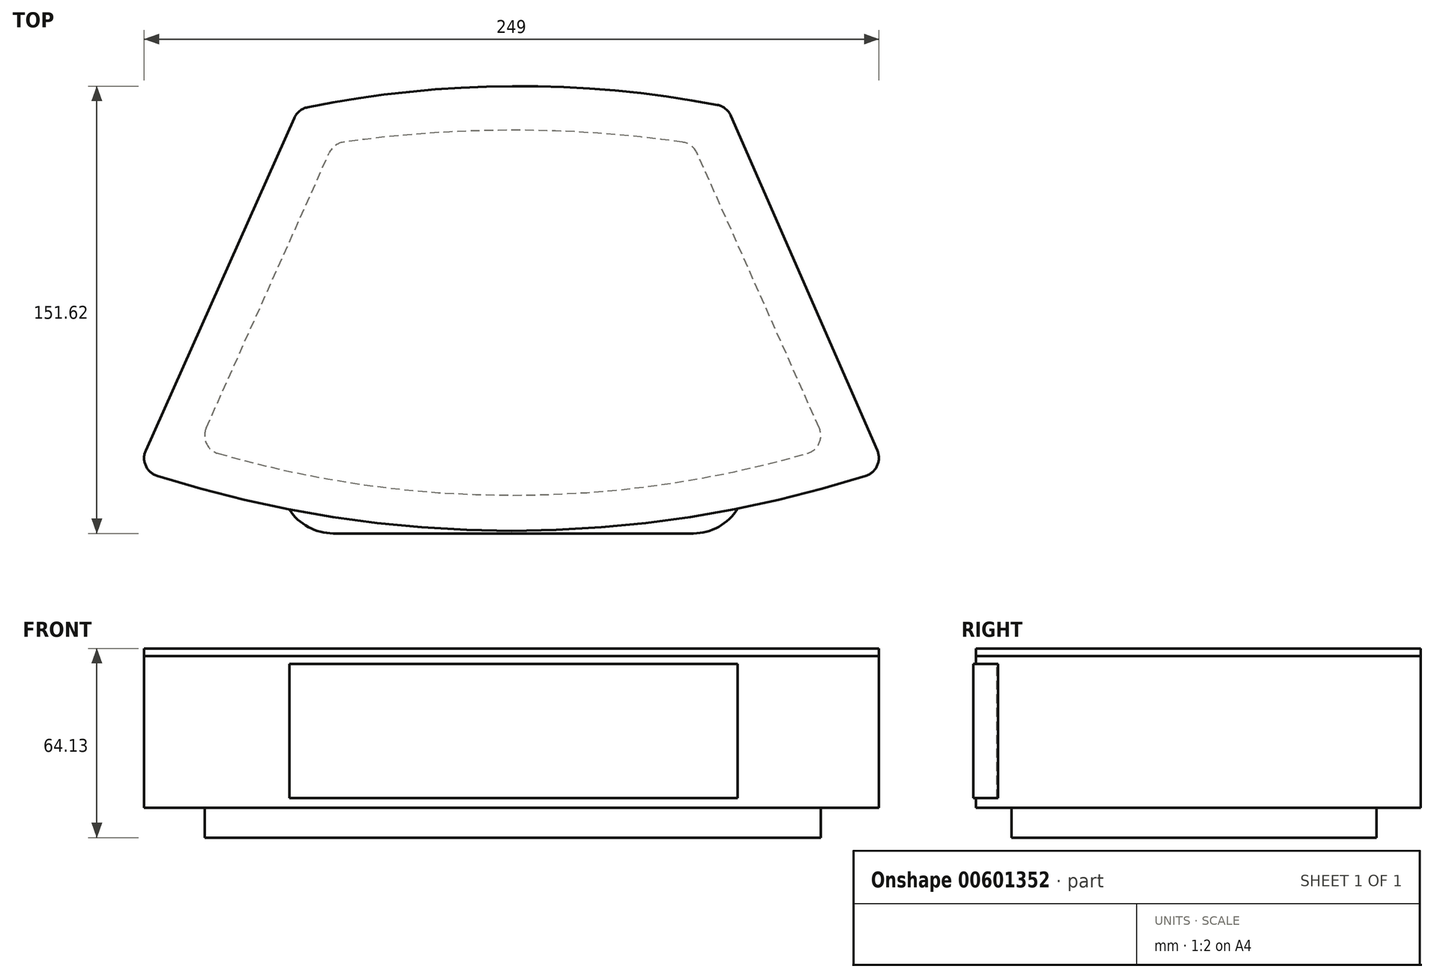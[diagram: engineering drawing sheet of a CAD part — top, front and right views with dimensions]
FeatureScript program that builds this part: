
annotation { "Feature Type Name" : "Feature", "Feature Type Description" : "" }
export const myFeature = defineFeature(function(context is Context, id is Id, definition is map)
    precondition{}
    {
        {
            var Q0;
            Q0=qCreatedBy(makeId("Top.planeOp"),FACE);
            var sketch = newSketch(context, id + "F0", { "sketchPlane" : qUnion([Q0])});
            skLineSegment(sketch, "E0", {"start": v(-72.1, 72.44) * mm, "end": v(-126.63, -49.66) * mm});
            skLineSegment(sketch, "E1", {"start": v(73.23, 73.26) * mm, "end": v(126.96, -49.66) * mm});
            skArc(sketch, "E2", {"start": v(-126.63, -49.66) * mm, "mid": v(0.16, -70.49) * mm, "end": v(126.96, -49.66) * mm});
            skArc(sketch, "E3", {"start": v(73.23, 73.26) * mm, "mid": v(0.52, 80.25) * mm, "end": v(-72.1, 72.44) * mm});
            skSolve(sketch);
        }
        {
            var Q0;
            Q0 = qSketchRegion(id + "F0", true);
            extrude(context, id + "F1", {"entities" : qUnion([Q0]), "oppositeDirection" : true, "depth" : 51.43 * mm, "offsetDistance" : 25.4 * mm});
        }
        {
            var Q0;
            Q0=makeQuery(id+"F1.opExtrude","CAP_FACE",FACE,{"disambiguationData":[OSD([sQuery(id+"F0.wireOp",EDGE,"E0"),sQuery(id+"F0.wireOp",EDGE,"E1"),sQuery(id+"F0.wireOp",EDGE,"E2"),sQuery(id+"F0.wireOp",EDGE,"E3")])],"isStart":false});
            var sketch = newSketch(context, id + "F2", { "sketchPlane" : qUnion([Q0])});
            skLineSegment(sketch, "E4", {"start": v(-106.2, 42.2) * mm, "end": v(-60.18, -60.78) * mm});
            skArc(sketch, "E5", {"start": v(-60.18, -60.78) * mm, "mid": v(0.75, -65.32) * mm, "end": v(61.68, -60.78) * mm});
            skLineSegment(sketch, "E6", {"start": v(107.41, 42.2) * mm, "end": v(61.68, -60.78) * mm});
            skArc(sketch, "E7", {"start": v(107.41, 42.2) * mm, "mid": v(0.6, 58.42) * mm, "end": v(-106.2, 42.2) * mm});
            skSolve(sketch);
        }
        {
            var Q0;
            Q0 = qSketchRegion(id + "F2", true);
            extrude(context, id + "F3", {"entities" : qUnion([Q0]), "depth" : 10.16 * mm, "offsetDistance" : 25.4 * mm});
        }
        {
            var Q0;
            Q0=makeQuery(id+"F1.opExtrude","CAP_FACE",FACE,{"disambiguationData":[OSD([sQuery(id+"F0.wireOp",EDGE,"E0"),sQuery(id+"F0.wireOp",EDGE,"E1"),sQuery(id+"F0.wireOp",EDGE,"E2"),sQuery(id+"F0.wireOp",EDGE,"E3")])],"isStart":true});
            var sketch = newSketch(context, id + "F4", { "sketchPlane" : qUnion([Q0])});
            skSolve(sketch);
        }
        {
            var Q0;
            Q0=makeQuery(id+"F4.imprint","IMPRINT",FACE,{"disambiguationData":[TD([[makeQuery(id+"F4.imprint","IMPRINT",EDGE,{"derivedFrom":makeQuery(id+"F1.opExtrude","CAP_EDGE",EDGE,{"disambiguationData":[OSD([sQuery(id+"F0.wireOp",EDGE,"E0")])],"isStart":true})}),1.0]])]});
            extrude(context, id + "F5", {"entities" : qUnion([Q0]), "depth" : 2.54 * mm, "offsetDistance" : 25.4 * mm});
        }
        {
            var Q0;
            Q0=makeQuery(id+"F1.opExtrude","SWEPT_EDGE",EDGE,{"disambiguationData":[OSD([sQuery(id+"F0.wireOp",EDGE,"E0"),sQuery(id+"F0.wireOp",EDGE,"E2")])]});
            var Q1;
            Q1=makeQuery(id+"F5.opExtrude","SWEPT_EDGE",EDGE,{"disambiguationData":[OSD([sQuery(id+"F0.wireOp",EDGE,"E0"),sQuery(id+"F0.wireOp",EDGE,"E2")])]});
            var Q2;
            Q2=makeQuery(id+"F3.opExtrude","SWEPT_EDGE",EDGE,{"disambiguationData":[OSD([sQuery(id+"F2.wireOp",EDGE,"E4"),sQuery(id+"F2.wireOp",EDGE,"E7")])]});
            var Q3;
            Q3=makeQuery(id+"F5.opExtrude","SWEPT_EDGE",EDGE,{"disambiguationData":[OSD([sQuery(id+"F0.wireOp",EDGE,"E1"),sQuery(id+"F0.wireOp",EDGE,"E2")])]});
            var Q4;
            Q4=makeQuery(id+"F1.opExtrude","SWEPT_EDGE",EDGE,{"disambiguationData":[OSD([sQuery(id+"F0.wireOp",EDGE,"E1"),sQuery(id+"F0.wireOp",EDGE,"E2")])]});
            var Q5;
            Q5=makeQuery(id+"F3.opExtrude","SWEPT_EDGE",EDGE,{"disambiguationData":[OSD([sQuery(id+"F2.wireOp",EDGE,"E6"),sQuery(id+"F2.wireOp",EDGE,"E7")])]});
            var Q6;
            Q6=makeQuery(id+"F5.opExtrude","SWEPT_EDGE",EDGE,{"disambiguationData":[OSD([sQuery(id+"F0.wireOp",EDGE,"E1"),sQuery(id+"F0.wireOp",EDGE,"E3")])]});
            var Q7;
            Q7=makeQuery(id+"F1.opExtrude","SWEPT_EDGE",EDGE,{"disambiguationData":[OSD([sQuery(id+"F0.wireOp",EDGE,"E1"),sQuery(id+"F0.wireOp",EDGE,"E3")])]});
            var Q8;
            Q8=makeQuery(id+"F3.opExtrude","SWEPT_EDGE",EDGE,{"disambiguationData":[OSD([sQuery(id+"F2.wireOp",EDGE,"E5"),sQuery(id+"F2.wireOp",EDGE,"E6")])]});
            var Q9;
            Q9=makeQuery(id+"F5.opExtrude","SWEPT_EDGE",EDGE,{"disambiguationData":[OSD([sQuery(id+"F0.wireOp",EDGE,"E0"),sQuery(id+"F0.wireOp",EDGE,"E3")])]});
            var Q10;
            Q10=makeQuery(id+"F1.opExtrude","SWEPT_EDGE",EDGE,{"disambiguationData":[OSD([sQuery(id+"F0.wireOp",EDGE,"E0"),sQuery(id+"F0.wireOp",EDGE,"E3")])]});
            var Q11;
            Q11=makeQuery(id+"F3.opExtrude","SWEPT_EDGE",EDGE,{"disambiguationData":[OSD([sQuery(id+"F2.wireOp",EDGE,"E4"),sQuery(id+"F2.wireOp",EDGE,"E5")])]});
            fillet(context, id + "F6", {"entities" : qUnion([Q0, Q1, Q2, Q3, Q4, Q5, Q6, Q7, Q8, Q9, Q10, Q11]), "radius" : 6.35 * mm, "tangentPropagation" : true, "allowEdgeOverflow" : false});
        }
        {
            var Q0;
            Q0=qCreatedBy(makeId("Front.planeOp"),FACE);
            var sketch = newSketch(context, id + "F7", { "sketchPlane" : qUnion([Q0])});
            skLineSegment(sketch, "E8", {"start": v(-75.07, -2.73) * mm, "end": v(-75.07, -48.2) * mm});
            skLineSegment(sketch, "E9", {"start": v(-75.07, -48.2) * mm, "end": v(76.89, -48.2) * mm});
            skLineSegment(sketch, "E10", {"start": v(76.89, -48.2) * mm, "end": v(76.89, -2.73) * mm});
            skLineSegment(sketch, "E11", {"start": v(76.89, -2.73) * mm, "end": v(-75.07, -2.73) * mm});
            skSolve(sketch);
        }
        {
            var Q0;
            Q0 = qSketchRegion(id + "F7", true);
            extrude(context, id + "F8", {"entities" : qUnion([Q0]), "operationType" : NewBodyOperationType.ADD, "depth" : 71.37 * mm, "offsetDistance" : 25.4 * mm});
        }
        {
            var Q0;
            Q0=makeQuery(id+"F8.opExtrude","CAP_EDGE",EDGE,{"disambiguationData":[OSD([sQuery(id+"F7.wireOp",EDGE,"E8")])],"isStart":false});
            var Q1;
            Q1=makeQuery(id+"F8.opExtrude","CAP_EDGE",EDGE,{"disambiguationData":[OSD([sQuery(id+"F7.wireOp",EDGE,"E10")])],"isStart":false});
            fillet(context, id + "F9", {"entities" : qUnion([Q0, Q1]), "radius" : 17.78 * mm, "tangentPropagation" : true, "allowEdgeOverflow" : false});
        }
    });
